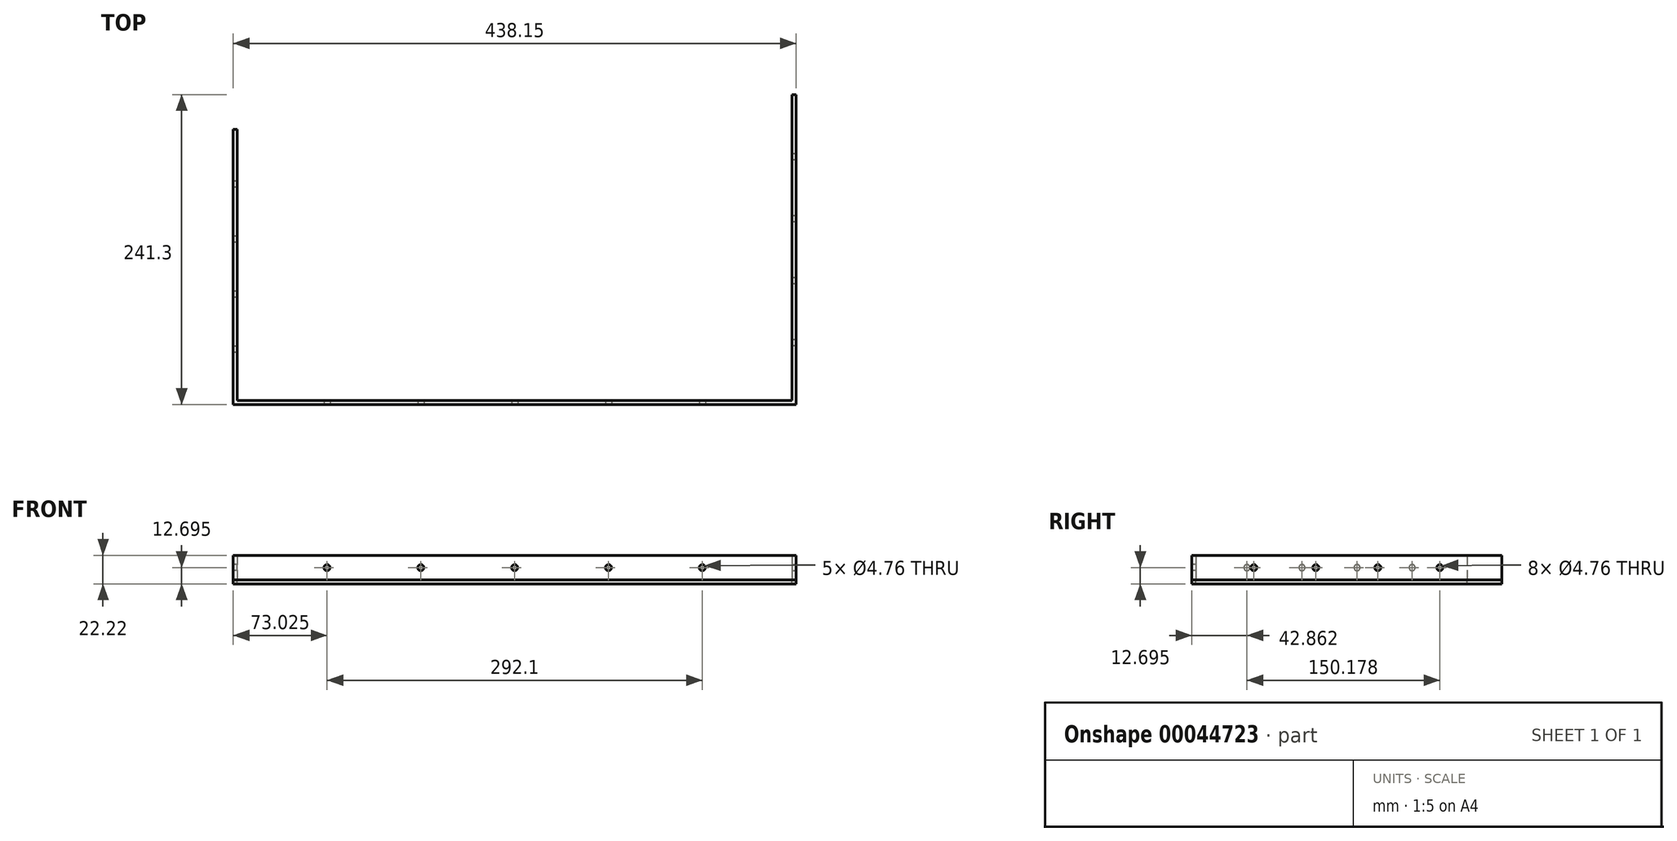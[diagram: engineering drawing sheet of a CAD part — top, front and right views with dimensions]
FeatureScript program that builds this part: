
annotation { "Feature Type Name" : "Feature", "Feature Type Description" : "" }
export const myFeature = defineFeature(function(context is Context, id is Id, definition is map)
    precondition{}
    {
        {
            var Q0;
            Q0=qCreatedBy(makeId("Top.planeOp"),FACE);
            var sketch = newSketch(context, id + "F0", { "sketchPlane" : qUnion([Q0])});
            skLineSegment(sketch, "E0", {"start": v(0, 0) * mm, "end": v(0, 214.31) * mm});
            skLineSegment(sketch, "E1", {"start": v(0, 214.31) * mm, "end": v(60.33, 214.31) * mm});
            skLineSegment(sketch, "E2", {"start": v(0, 0) * mm, "end": v(438.15, 0) * mm});
            skLineSegment(sketch, "E3", {"start": v(438.15, 0) * mm, "end": v(438.15, 241.3) * mm});
            skLineSegment(sketch, "E4", {"start": v(60.33, 214.31) * mm, "end": v(60.33, 241.3) * mm});
            skLineSegment(sketch, "E5", {"start": v(60.33, 241.3) * mm, "end": v(259.14, 241.3) * mm});
            skLineSegment(sketch, "E6", {"start": v(259.14, 241.3) * mm, "end": v(259.14, 222.25) * mm});
            skLineSegment(sketch, "E7", {"start": v(438.15, 241.3) * mm, "end": v(306.39, 241.3) * mm});
            skLineSegment(sketch, "E8", {"start": v(306.39, 241.3) * mm, "end": v(306.39, 222.25) * mm});
            skLineSegment(sketch, "E9", {"start": v(306.39, 222.25) * mm, "end": v(259.14, 222.25) * mm});
            skLineSegment(sketch, "E10", {"start": v(0, 214.31) * mm, "end": v(3.17, 214.31) * mm});
            skLineSegment(sketch, "E11", {"start": v(3.17, 214.31) * mm, "end": v(3.17, 3.17) * mm});
            skLineSegment(sketch, "E12", {"start": v(3.17, 3.17) * mm, "end": v(434.98, 3.17) * mm});
            skLineSegment(sketch, "E13", {"start": v(434.98, 3.17) * mm, "end": v(434.98, 241.3) * mm});
            skLineSegment(sketch, "E14", {"start": v(434.98, 241.3) * mm, "end": v(438.15, 241.3) * mm});
            skLineSegment(sketch, "E15", {"start": v(211.97, 3.17) * mm, "end": v(211.97, 0) * mm, "construction": true});
            skPoint(sketch, "E15.endSnap0", {"position": v(219.08, 0) * mm});
            skLineSegment(sketch, "E16", {"start": v(438.15, 241.3) * mm, "end": v(434.98, 241.3) * mm});
            skLineSegment(sketch, "E17", {"start": v(60.33, 214.31) * mm, "end": v(60.33, 205.42) * mm, "construction": true});
            skLineSegment(sketch, "E18", {"start": v(60.33, 205.42) * mm, "end": v(34.92, 205.42) * mm, "construction": true});
            skLineSegment(sketch, "E19", {"start": v(34.92, 205.42) * mm, "end": v(11.11, 205.42) * mm, "construction": true});
            skLineSegment(sketch, "E20", {"start": v(60.33, 205.42) * mm, "end": v(136.53, 205.42) * mm, "construction": true});
            skLineSegment(sketch, "E21", {"start": v(60.33, 205.42) * mm, "end": v(60.33, 164.15) * mm, "construction": true});
            skLineSegment(sketch, "E22", {"start": v(60.33, 164.15) * mm, "end": v(34.92, 164.15) * mm, "construction": true});
            skLineSegment(sketch, "E23", {"start": v(34.92, 164.15) * mm, "end": v(34.92, 205.42) * mm, "construction": true});
            skLineSegment(sketch, "E24", {"start": v(34.92, 164.15) * mm, "end": v(11.11, 164.15) * mm, "construction": true});
            skLineSegment(sketch, "E25", {"start": v(11.11, 164.15) * mm, "end": v(11.11, 205.42) * mm, "construction": true});
            skCircle(sketch, "E26", {"center": v(34.92, 205.42) * mm, "radius": 2.38 * mm});
            skCircle(sketch, "E27", {"center": v(11.11, 205.42) * mm, "radius": 2.38 * mm});
            skCircle(sketch, "E28", {"center": v(11.11, 164.15) * mm, "radius": 2.38 * mm});
            skCircle(sketch, "E29", {"center": v(34.92, 164.15) * mm, "radius": 2.38 * mm});
            skLineSegment(sketch, "E30", {"start": v(60.33, 164.15) * mm, "end": v(136.53, 164.15) * mm, "construction": true});
            skLineSegment(sketch, "E31", {"start": v(136.53, 205.42) * mm, "end": v(136.53, 164.15) * mm, "construction": true});
            skCircle(sketch, "E32", {"center": v(136.53, 205.42) * mm, "radius": 2.38 * mm});
            skCircle(sketch, "E33", {"center": v(136.53, 164.15) * mm, "radius": 2.38 * mm});
            skSolve(sketch);
        }
        {
            var Q0;
            Q0=makeQuery(id+"F0.imprint","IMPRINT",FACE,{"disambiguationData":[TD([[makeQuery(id+"F0.imprint","IMPRINT",EDGE,{"derivedFrom":sQuery(id+"F0.wireOp",EDGE,"E0")}),-1.0]])]});
            var Q1;
            Q1=sQuery(id+"F0.wireOp",EDGE,"E11");
            var Q2;
            Q2=sQuery(id+"F0.wireOp",EDGE,"E10");
            var Q3;
            Q3=sQuery(id+"F0.wireOp",EDGE,"E0");
            var Q4;
            Q4=sQuery(id+"F0.wireOp",EDGE,"E2");
            var Q5;
            Q5=sQuery(id+"F0.wireOp",EDGE,"E12");
            var Q6;
            Q6=sQuery(id+"F0.wireOp",EDGE,"E3");
            var Q7;
            Q7=sQuery(id+"F0.wireOp",EDGE,"E13");
            var Q8;
            Q8=sQuery(id+"F0.wireOp",EDGE,"E16");
            extrude(context, id + "F1", {"entities" : qUnion([Q0]), "surfaceEntities" : qUnion([Q1, Q2, Q3, Q4, Q5, Q6, Q7, Q8]), "depth" : 19.05 * mm});
        }
        {
            var Q0;
            Q0=makeQuery(id+"F0.imprint","IMPRINT",FACE,{"disambiguationData":[TD([[makeQuery(id+"F0.imprint","IMPRINT",EDGE,{"derivedFrom":sQuery(id+"F0.wireOp",EDGE,"E1")}),-1.0]])]});
            var Q1;
            Q1=makeQuery(id+"F0.imprint","IMPRINT",FACE,{"disambiguationData":[TD([[makeQuery(id+"F0.imprint","IMPRINT",EDGE,{"derivedFrom":sQuery(id+"F0.wireOp",EDGE,"E0")}),-1.0]])]});
            extrude(context, id + "F2", {"entities" : qUnion([Q0, Q1]), "oppositeDirection" : true, "depth" : 3.17 * mm});
        }
        {
            var Q0;
            Q0=makeQuery(id+"F1.opExtrude","SWEPT_FACE",FACE,{"disambiguationData":[OSD([sQuery(id+"F0.wireOp",EDGE,"E0")])]});
            var sketch = newSketch(context, id + "F3", { "sketchPlane" : qUnion([Q0])});
            skLineSegment(sketch, "E34", {"start": v(-214.31, 9.53) * mm, "end": v(-171.45, 9.53) * mm, "construction": true});
            skLineSegment(sketch, "E35", {"start": v(-171.45, 9.53) * mm, "end": v(-128.59, 9.53) * mm, "construction": true});
            skLineSegment(sketch, "E36", {"start": v(-128.59, 9.53) * mm, "end": v(-85.73, 9.53) * mm, "construction": true});
            skLineSegment(sketch, "E37", {"start": v(-85.73, 9.53) * mm, "end": v(-42.86, 9.53) * mm, "construction": true});
            skLineSegment(sketch, "E38", {"start": v(-42.86, 9.53) * mm, "end": v(0, 9.53) * mm, "construction": true});
            skCircle(sketch, "E39", {"center": v(-171.45, 9.53) * mm, "radius": 2.38 * mm});
            skCircle(sketch, "E40", {"center": v(-128.59, 9.53) * mm, "radius": 2.38 * mm});
            skCircle(sketch, "E41", {"center": v(-85.73, 9.53) * mm, "radius": 2.38 * mm});
            skCircle(sketch, "E42", {"center": v(-42.86, 9.53) * mm, "radius": 2.38 * mm});
            skSolve(sketch);
        }
        {
            var Q0;
            Q0=makeQuery(id+"F3.imprint","IMPRINT",FACE,{"disambiguationData":[TD([[makeQuery(id+"F3.imprint","IMPRINT",EDGE,{"derivedFrom":sQuery(id+"F3.wireOp",EDGE,"E39")}),1.0]])]});
            var Q1;
            Q1=makeQuery(id+"F3.imprint","IMPRINT",FACE,{"disambiguationData":[TD([[makeQuery(id+"F3.imprint","IMPRINT",EDGE,{"derivedFrom":sQuery(id+"F3.wireOp",EDGE,"E40")}),1.0]])]});
            var Q2;
            Q2=makeQuery(id+"F3.imprint","IMPRINT",FACE,{"disambiguationData":[TD([[makeQuery(id+"F3.imprint","IMPRINT",EDGE,{"derivedFrom":sQuery(id+"F3.wireOp",EDGE,"E41")}),1.0]])]});
            var Q3;
            Q3=makeQuery(id+"F3.imprint","IMPRINT",FACE,{"disambiguationData":[TD([[makeQuery(id+"F3.imprint","IMPRINT",EDGE,{"derivedFrom":sQuery(id+"F3.wireOp",EDGE,"E42")}),1.0]])]});
            extrude(context, id + "F4", {"entities" : qUnion([Q0, Q1, Q2, Q3]), "operationType" : NewBodyOperationType.REMOVE, "oppositeDirection" : true, "depth" : 12.7 * mm});
        }
        {
            var Q0;
            Q0=makeQuery(id+"F1.opExtrude","SWEPT_FACE",FACE,{"disambiguationData":[OSD([sQuery(id+"F0.wireOp",EDGE,"E2")])]});
            var sketch = newSketch(context, id + "F5", { "sketchPlane" : qUnion([Q0])});
            skLineSegment(sketch, "E43", {"start": v(0, 9.53) * mm, "end": v(73.02, 9.53) * mm, "construction": true});
            skLineSegment(sketch, "E44", {"start": v(73.02, 9.53) * mm, "end": v(146.05, 9.53) * mm, "construction": true});
            skLineSegment(sketch, "E45", {"start": v(146.05, 9.53) * mm, "end": v(219.08, 9.53) * mm, "construction": true});
            skLineSegment(sketch, "E46", {"start": v(219.08, 9.53) * mm, "end": v(292.1, 9.53) * mm, "construction": true});
            skLineSegment(sketch, "E47", {"start": v(292.1, 9.53) * mm, "end": v(365.13, 9.53) * mm, "construction": true});
            skLineSegment(sketch, "E48", {"start": v(365.13, 9.53) * mm, "end": v(438.15, 9.53) * mm, "construction": true});
            skCircle(sketch, "E49", {"center": v(73.02, 9.53) * mm, "radius": 2.38 * mm});
            skCircle(sketch, "E50", {"center": v(146.05, 9.53) * mm, "radius": 2.38 * mm});
            skCircle(sketch, "E51", {"center": v(219.08, 9.53) * mm, "radius": 2.38 * mm});
            skCircle(sketch, "E52", {"center": v(292.1, 9.53) * mm, "radius": 2.38 * mm});
            skCircle(sketch, "E53", {"center": v(365.13, 9.53) * mm, "radius": 2.38 * mm});
            skSolve(sketch);
        }
        {
            var Q0;
            Q0=makeQuery(id+"F5.imprint","IMPRINT",FACE,{"disambiguationData":[TD([[makeQuery(id+"F5.imprint","IMPRINT",EDGE,{"derivedFrom":sQuery(id+"F5.wireOp",EDGE,"E49")}),1.0]])]});
            var Q1;
            Q1=makeQuery(id+"F5.imprint","IMPRINT",FACE,{"disambiguationData":[TD([[makeQuery(id+"F5.imprint","IMPRINT",EDGE,{"derivedFrom":sQuery(id+"F5.wireOp",EDGE,"E50")}),1.0]])]});
            var Q2;
            Q2=makeQuery(id+"F5.imprint","IMPRINT",FACE,{"disambiguationData":[TD([[makeQuery(id+"F5.imprint","IMPRINT",EDGE,{"derivedFrom":sQuery(id+"F5.wireOp",EDGE,"E51")}),1.0]])]});
            var Q3;
            Q3=makeQuery(id+"F5.imprint","IMPRINT",FACE,{"disambiguationData":[TD([[makeQuery(id+"F5.imprint","IMPRINT",EDGE,{"derivedFrom":sQuery(id+"F5.wireOp",EDGE,"E52")}),1.0]])]});
            var Q4;
            Q4=makeQuery(id+"F5.imprint","IMPRINT",FACE,{"disambiguationData":[TD([[makeQuery(id+"F5.imprint","IMPRINT",EDGE,{"derivedFrom":sQuery(id+"F5.wireOp",EDGE,"E53")}),1.0]])]});
            extrude(context, id + "F6", {"entities" : qUnion([Q0, Q1, Q2, Q3, Q4]), "operationType" : NewBodyOperationType.REMOVE, "oppositeDirection" : true, "depth" : 12.7 * mm});
        }
        {
            var Q0;
            Q0=makeQuery(id+"F1.opExtrude","SWEPT_FACE",FACE,{"disambiguationData":[OSD([sQuery(id+"F0.wireOp",EDGE,"E3")])]});
            var sketch = newSketch(context, id + "F7", { "sketchPlane" : qUnion([Q0])});
            skLineSegment(sketch, "E54", {"start": v(0, 9.53) * mm, "end": v(48.26, 9.53) * mm, "construction": true});
            skLineSegment(sketch, "E55", {"start": v(48.26, 9.53) * mm, "end": v(96.52, 9.53) * mm, "construction": true});
            skLineSegment(sketch, "E56", {"start": v(96.52, 9.53) * mm, "end": v(144.78, 9.53) * mm, "construction": true});
            skLineSegment(sketch, "E57", {"start": v(144.78, 9.53) * mm, "end": v(193.04, 9.53) * mm, "construction": true});
            skLineSegment(sketch, "E58", {"start": v(193.04, 9.53) * mm, "end": v(241.3, 9.53) * mm, "construction": true});
            skCircle(sketch, "E59", {"center": v(48.26, 9.53) * mm, "radius": 2.38 * mm});
            skCircle(sketch, "E60", {"center": v(96.52, 9.53) * mm, "radius": 2.38 * mm});
            skCircle(sketch, "E61", {"center": v(144.78, 9.53) * mm, "radius": 2.38 * mm});
            skCircle(sketch, "E62", {"center": v(193.04, 9.53) * mm, "radius": 2.38 * mm});
            skSolve(sketch);
        }
        {
            var Q0;
            Q0 = qSketchRegion(id + "F7", true);
            extrude(context, id + "F8", {"entities" : qUnion([Q0]), "operationType" : NewBodyOperationType.REMOVE, "oppositeDirection" : true, "depth" : 12.7 * mm});
        }
    });
